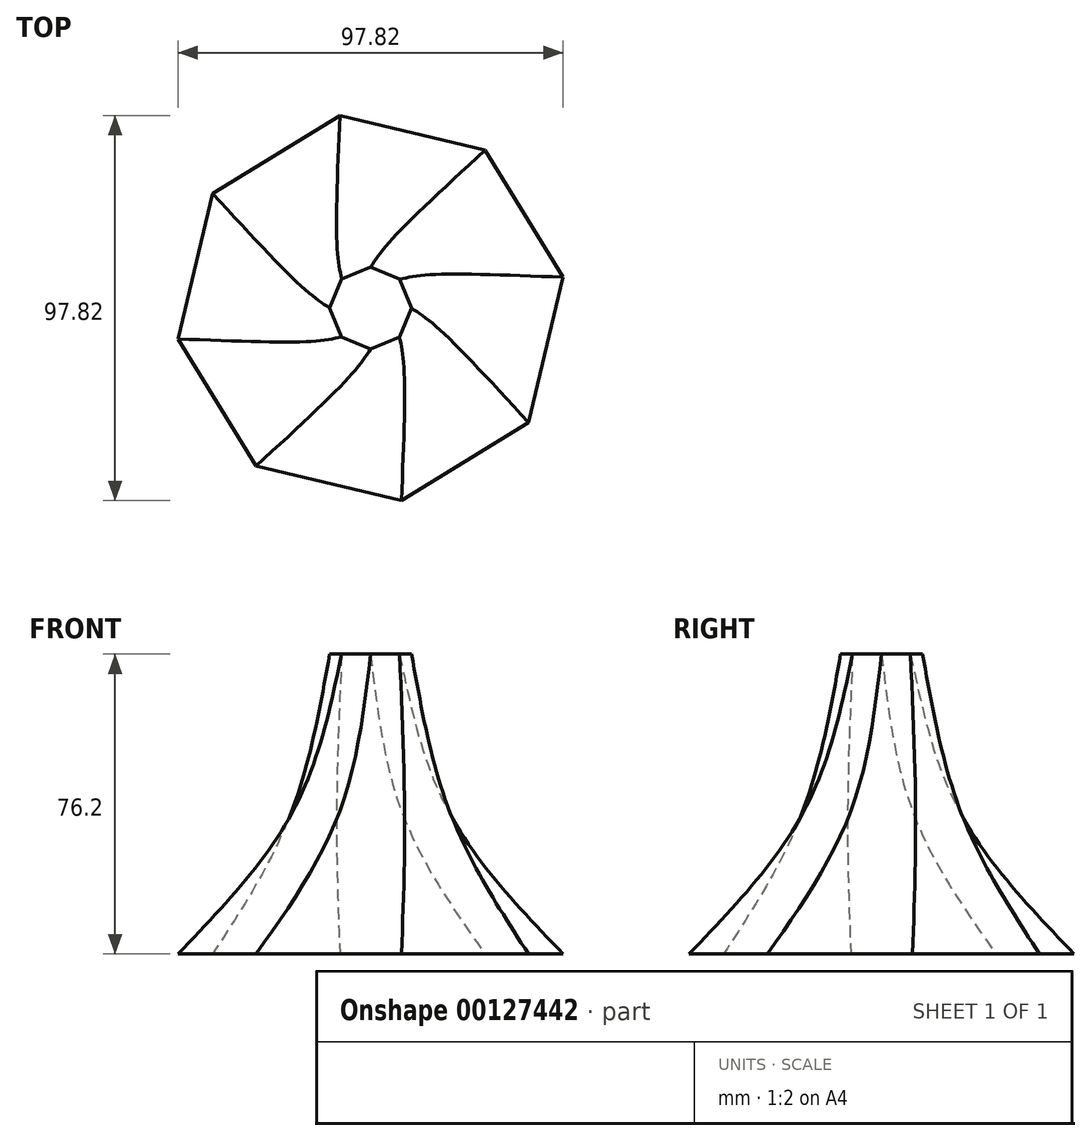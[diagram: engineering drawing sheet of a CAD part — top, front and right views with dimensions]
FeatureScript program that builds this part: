
annotation { "Feature Type Name" : "Feature", "Feature Type Description" : "" }
export const myFeature = defineFeature(function(context is Context, id is Id, definition is map)
    precondition{}
    {
        {
            var Q0;
            Q0=qCreatedBy(makeId("Top.planeOp"),FACE);
            cPlane(context, id + "F0", {"entities" : qUnion([Q0]), "cplaneType" : CPlaneType.OFFSET, "offset" : 38.1 * mm, "width" : 152.4 * mm, "height" : 152.4 * mm});
        }
        {
            var Q0;
            Q0=qCreatedBy(makeId("Top.planeOp"),FACE);
            cPlane(context, id + "F1", {"entities" : qUnion([Q0]), "cplaneType" : CPlaneType.OFFSET, "offset" : 38.1 * mm, "oppositeDirection" : true, "width" : 152.4 * mm, "height" : 152.4 * mm});
        }
        {
            var Q0;
            Q0=qCreatedBy(id+"F1.planeOp",FACE);
            var sketch = newSketch(context, id + "F2", { "sketchPlane" : qUnion([Q0])});
            skCircle(sketch, "E0.cCircle", {"center": v(0, 0) * mm, "radius": 45.76 * mm, "construction": true});
            skLineSegment(sketch, "E0.0", {"start": v(-40.12, 29.05) * mm, "end": v(-7.83, 48.9) * mm});
            skLineSegment(sketch, "E0.1", {"start": v(-7.83, 48.9) * mm, "end": v(29.05, 40.12) * mm});
            skLineSegment(sketch, "E0.2", {"start": v(29.05, 40.12) * mm, "end": v(48.9, 7.83) * mm});
            skLineSegment(sketch, "E0.3", {"start": v(48.9, 7.83) * mm, "end": v(40.12, -29.05) * mm});
            skLineSegment(sketch, "E0.4", {"start": v(40.12, -29.05) * mm, "end": v(7.83, -48.9) * mm});
            skLineSegment(sketch, "E0.5", {"start": v(7.83, -48.9) * mm, "end": v(-29.05, -40.12) * mm});
            skLineSegment(sketch, "E0.6", {"start": v(-29.05, -40.12) * mm, "end": v(-48.9, -7.83) * mm});
            skLineSegment(sketch, "E0.7", {"start": v(-48.9, -7.83) * mm, "end": v(-40.12, 29.05) * mm});
            skPoint(sketch, "E0.0.midPoint", {"position": v(-23.97, 38.98) * mm});
            skSolve(sketch);
        }
        {
            var Q0;
            Q0=qCreatedBy(id+"F0.planeOp",FACE);
            var sketch = newSketch(context, id + "F3", { "sketchPlane" : qUnion([Q0])});
            skCircle(sketch, "E1.cCircle", {"center": v(0, 0) * mm, "radius": 9.6 * mm, "construction": true});
            skLineSegment(sketch, "E1.0", {"start": v(-10.4, 0) * mm, "end": v(-7.35, 7.35) * mm});
            skLineSegment(sketch, "E1.1", {"start": v(-7.35, 7.35) * mm, "end": v(0, 10.4) * mm});
            skLineSegment(sketch, "E1.2", {"start": v(0, 10.4) * mm, "end": v(7.35, 7.35) * mm});
            skLineSegment(sketch, "E1.3", {"start": v(7.35, 7.35) * mm, "end": v(10.4, 0) * mm});
            skLineSegment(sketch, "E1.4", {"start": v(10.4, 0) * mm, "end": v(7.35, -7.35) * mm});
            skLineSegment(sketch, "E1.5", {"start": v(7.35, -7.35) * mm, "end": v(0, -10.4) * mm});
            skLineSegment(sketch, "E1.6", {"start": v(0, -10.4) * mm, "end": v(-7.35, -7.35) * mm});
            skLineSegment(sketch, "E1.7", {"start": v(-7.35, -7.35) * mm, "end": v(-10.4, 0) * mm});
            skPoint(sketch, "E1.0.midPoint", {"position": v(-8.88, 3.68) * mm});
            skSolve(sketch);
        }
        {
            var Q0;
            Q0=qCreatedBy(makeId("Top.planeOp"),FACE);
            var sketch = newSketch(context, id + "F4", { "sketchPlane" : qUnion([Q0])});
            skCircle(sketch, "E2.cCircle", {"center": v(0, 0) * mm, "radius": 19.1 * mm, "construction": true});
            skLineSegment(sketch, "E2.0", {"start": v(7.2, 19.38) * mm, "end": v(18.8, 8.62) * mm});
            skLineSegment(sketch, "E2.1", {"start": v(18.8, 8.62) * mm, "end": v(19.38, -7.2) * mm});
            skLineSegment(sketch, "E2.2", {"start": v(19.38, -7.2) * mm, "end": v(8.62, -18.8) * mm});
            skLineSegment(sketch, "E2.3", {"start": v(8.62, -18.8) * mm, "end": v(-7.2, -19.38) * mm});
            skLineSegment(sketch, "E2.4", {"start": v(-7.2, -19.38) * mm, "end": v(-18.8, -8.62) * mm});
            skLineSegment(sketch, "E2.5", {"start": v(-18.8, -8.62) * mm, "end": v(-19.38, 7.2) * mm});
            skLineSegment(sketch, "E2.6", {"start": v(-19.38, 7.2) * mm, "end": v(-8.62, 18.8) * mm});
            skLineSegment(sketch, "E2.7", {"start": v(-8.62, 18.8) * mm, "end": v(7.2, 19.38) * mm});
            skPoint(sketch, "E2.0.midPoint", {"position": v(13, 14) * mm});
            skSolve(sketch);
        }
        {
            var Q0;
            Q0=makeQuery(id+"F3.imprint","IMPRINT",FACE,{"disambiguationData":[TD([[makeQuery(id+"F3.imprint","IMPRINT",EDGE,{"derivedFrom":sQuery(id+"F3.wireOp",EDGE,"E1.0")}),-1.0]])]});
            var Q1;
            Q1=makeQuery(id+"F4.imprint","IMPRINT",FACE,{"disambiguationData":[TD([[makeQuery(id+"F4.imprint","IMPRINT",EDGE,{"derivedFrom":sQuery(id+"F4.wireOp",EDGE,"E2.0")}),-1.0]])]});
            var Q2;
            Q2=makeQuery(id+"F2.imprint","IMPRINT",FACE,{"disambiguationData":[TD([[makeQuery(id+"F2.imprint","IMPRINT",EDGE,{"derivedFrom":sQuery(id+"F2.wireOp",EDGE,"E0.0")}),-1.0]])]});
            loft(context, id + "F5", {"sheetProfilesArray" : [{ "sheetProfileEntities" : qUnion([Q0]) }, { "sheetProfileEntities" : qUnion([Q1]) }, { "sheetProfileEntities" : qUnion([Q2]) }]});
        }
    });
